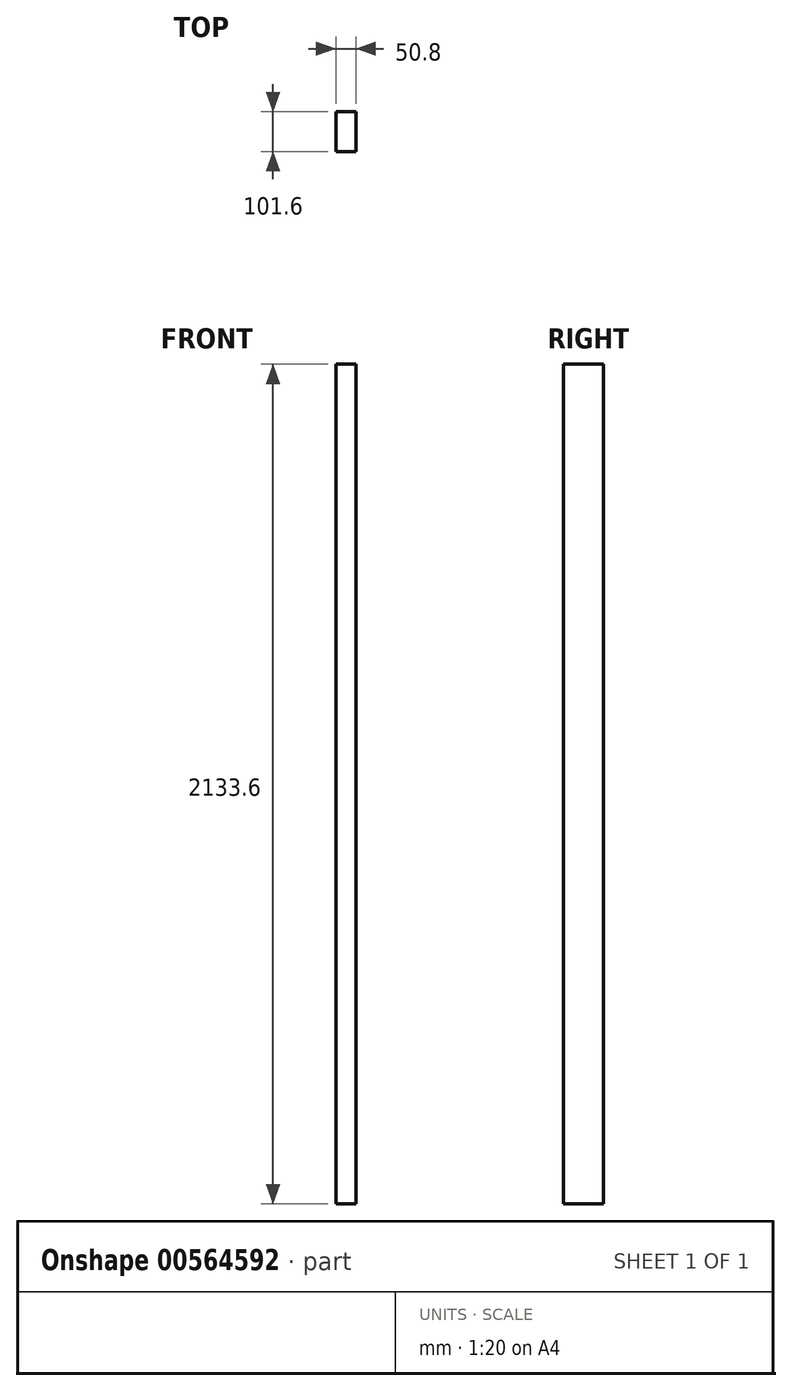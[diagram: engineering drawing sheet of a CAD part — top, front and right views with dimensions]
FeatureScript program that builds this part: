
annotation { "Feature Type Name" : "Feature", "Feature Type Description" : "" }
export const myFeature = defineFeature(function(context is Context, id is Id, definition is map)
    precondition{}
    {
        {
            var Q0;
            Q0=qCreatedBy(makeId("Top.planeOp"),FACE);
            var sketch = newSketch(context, id + "F0", { "sketchPlane" : qUnion([Q0])});
            skLineSegment(sketch, "E0.bottom", {"start": v(-26.23, 45.22) * mm, "end": v(24.57, 45.22) * mm});
            skLineSegment(sketch, "E0.top", {"start": v(-26.23, -56.38) * mm, "end": v(24.57, -56.38) * mm});
            skLineSegment(sketch, "E0.left", {"start": v(-26.23, 45.22) * mm, "end": v(-26.23, -56.38) * mm});
            skLineSegment(sketch, "E0.right", {"start": v(24.57, 45.22) * mm, "end": v(24.57, -56.38) * mm});
            skSolve(sketch);
        }
        {
            var Q0;
            Q0 = qSketchRegion(id + "F0", true);
            extrude(context, id + "F1", {"entities" : qUnion([Q0]), "depth" : 2133.6 * mm, "offsetDistance" : 25.4 * mm});
        }
    });
